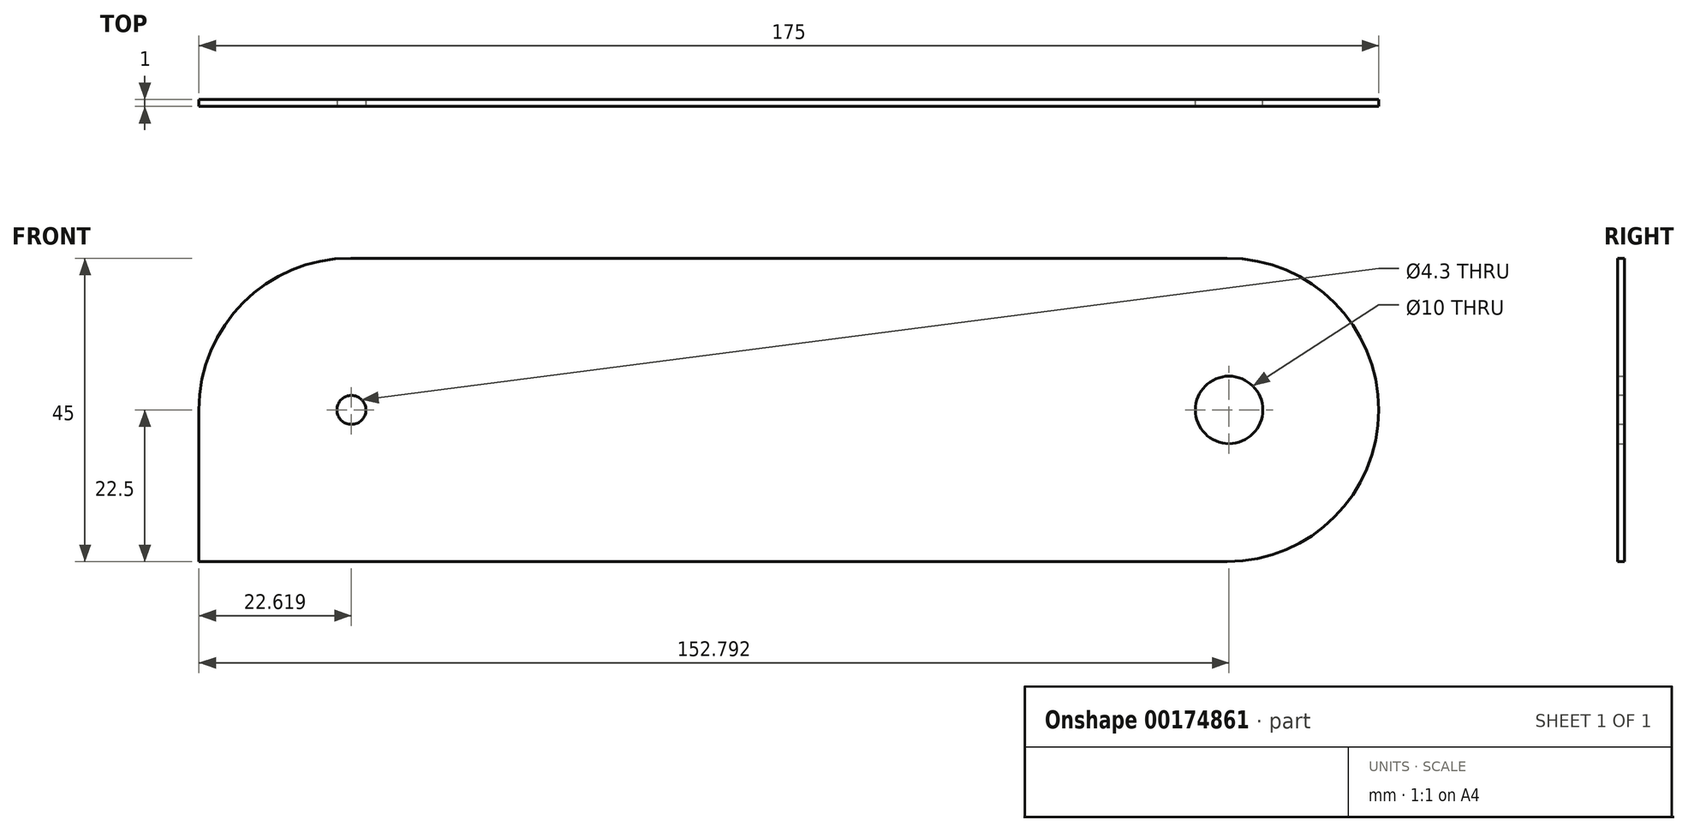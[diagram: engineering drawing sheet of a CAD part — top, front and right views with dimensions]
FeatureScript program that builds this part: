
annotation { "Feature Type Name" : "Feature", "Feature Type Description" : "" }
export const myFeature = defineFeature(function(context is Context, id is Id, definition is map)
    precondition{}
    {
        {
            var Q0;
            Q0=qCreatedBy(makeId("Front.planeOp"),FACE);
            var sketch = newSketch(context, id + "F0", { "sketchPlane" : qUnion([Q0])});
            skLineSegment(sketch, "E0.bottom", {"start": v(82.5, 22.5) * mm, "end": v(-82.5, 22.5) * mm});
            skLineSegment(sketch, "E0.top", {"start": v(82.5, -22.5) * mm, "end": v(-82.5, -22.5) * mm});
            skLineSegment(sketch, "E0.left", {"start": v(82.5, 22.5) * mm, "end": v(82.5, -22.5) * mm});
            skLineSegment(sketch, "E0.right", {"start": v(-82.5, 22.5) * mm, "end": v(-82.5, -22.5) * mm});
            skPoint(sketch, "E0.middle", {"position": v(0, 0) * mm});
            skCircle(sketch, "E1", {"center": v(-65, 0) * mm, "radius": 12.5 * mm});
            skCircle(sketch, "E2", {"center": v(65, 0) * mm, "radius": 12.5 * mm});
            skSolve(sketch);
        }
        {
            var Q0;
            Q0=qSketchRegion(id+"F0",true);
            extrude(context, id + "F1", {"entities" : qUnion([Q0]), "depth" : 1 * mm});
        }
        {
            var Q0;
            Q0=makeQuery(id+"F1.opExtrude","CAP_FACE",FACE,{"disambiguationData":[OSD([sQuery(id+"F0.wireOp",EDGE,"E0.bottom"),sQuery(id+"F0.wireOp",EDGE,"E0.top"),sQuery(id+"F0.wireOp",EDGE,"E0.left"),sQuery(id+"F0.wireOp",EDGE,"E0.right"),sQuery(id+"F0.wireOp",EDGE,"E1"),sQuery(id+"F0.wireOp",EDGE,"E2")])],"isStart":false});
            var sketch = newSketch(context, id + "F2", { "sketchPlane" : qUnion([Q0])});
            skArc(sketch, "E3", {"start": v(65, -22.5) * mm, "mid": v(87.5, 0) * mm, "end": v(65, 22.5) * mm});
            skPoint(sketch, "E4.end.orphan", {"position": v(-82.5, 0) * mm});
            skArc(sketch, "E5", {"start": v(-65, 22.5) * mm, "mid": v(-87.5, 0) * mm, "end": v(-65, -22.5) * mm});
            skLineSegment(sketch, "E6", {"start": v(-65, 22.5) * mm, "end": v(-65, 14.96) * mm});
            skLineSegment(sketch, "E7", {"start": v(-65, 14.96) * mm, "end": v(-75.45, 11.76) * mm});
            skLineSegment(sketch, "E8", {"start": v(-75.45, 11.76) * mm, "end": v(-79.56, 6.47) * mm});
            skLineSegment(sketch, "E9", {"start": v(-79.56, 6.47) * mm, "end": v(-79.56, 0) * mm});
            skLineSegment(sketch, "E10", {"start": v(-79.56, 0) * mm, "end": v(-76.59, -7.8) * mm});
            skLineSegment(sketch, "E11", {"start": v(-76.59, -7.8) * mm, "end": v(-72.84, -12.91) * mm});
            skLineSegment(sketch, "E12", {"start": v(-72.84, -12.91) * mm, "end": v(-67.48, -15.7) * mm});
            skLineSegment(sketch, "E13", {"start": v(-67.48, -15.7) * mm, "end": v(-65, -22.5) * mm});
            skLineSegment(sketch, "E14", {"start": v(65, 22.5) * mm, "end": v(71.47, 16.28) * mm});
            skLineSegment(sketch, "E15", {"start": v(71.47, 16.28) * mm, "end": v(77.4, 9.11) * mm});
            skLineSegment(sketch, "E16", {"start": v(77.4, 9.11) * mm, "end": v(80.4, 2.14) * mm});
            skLineSegment(sketch, "E17", {"start": v(80.4, 2.14) * mm, "end": v(80.4, -5.23) * mm});
            skLineSegment(sketch, "E18", {"start": v(80.4, -5.23) * mm, "end": v(78.4, -12.15) * mm});
            skLineSegment(sketch, "E19", {"start": v(78.4, -12.15) * mm, "end": v(74.66, -14.4) * mm});
            skLineSegment(sketch, "E20", {"start": v(74.66, -14.4) * mm, "end": v(68.4, -19.1) * mm});
            skLineSegment(sketch, "E21", {"start": v(68.4, -19.1) * mm, "end": v(65, -22.5) * mm});
            skSolve(sketch);
        }
        {
            var Q0;
            Q0=qSketchRegion(id+"F2",true);
            extrude(context, id + "F3", {"entities" : qUnion([Q0]), "operationType" : NewBodyOperationType.ADD, "oppositeDirection" : true, "depth" : 1 * mm});
        }
        {
            var Q0;
            {var subQ1=makeQuery(id+"F1.opExtrude","CAP_EDGE",EDGE,{"disambiguationData":[OSD([sQuery(id+"F0.wireOp",EDGE,"E0.bottom")])],"isStart":false});var subQ3=makeQuery(id+"F1.opExtrude","CAP_EDGE",EDGE,{"disambiguationData":[OSD([sQuery(id+"F0.wireOp",EDGE,"E0.right")])],"isStart":false});var subQ5=makeQuery(id+"F2.imprint","INTERSECT",VERTEX,{"derivedFrom":[subQ1,subQ3]});Q0=makeQuery(id+"F2.imprint","IMPRINT",FACE,{"disambiguationData":[TD([[makeQuery(id+"F2.imprint","IMPRINT",EDGE,{"disambiguationData":[TD([[subQ5,-1.0]])],"derivedFrom":subQ3}),1.0]])]});}
            extrude(context, id + "F4", {"entities" : qUnion([Q0]), "operationType" : NewBodyOperationType.REMOVE, "oppositeDirection" : true, "depth" : 25 * mm});
        }
        {
            var Q0;
            {var subQ1=makeQuery(id+"F1.opExtrude","CAP_EDGE",EDGE,{"disambiguationData":[OSD([sQuery(id+"F0.wireOp",EDGE,"E0.top")])],"isStart":false});var subQ3=makeQuery(id+"F1.opExtrude","CAP_EDGE",EDGE,{"disambiguationData":[OSD([sQuery(id+"F0.wireOp",EDGE,"E0.left")])],"isStart":false});var subQ5=makeQuery(id+"F2.imprint","INTERSECT",VERTEX,{"derivedFrom":[subQ1,subQ3]});Q0=makeQuery(id+"F2.imprint","IMPRINT",FACE,{"disambiguationData":[TD([[makeQuery(id+"F2.imprint","IMPRINT",EDGE,{"disambiguationData":[TD([[subQ5,1.0]])],"derivedFrom":subQ3}),-1.0]])]});}
            var Q1;
            {var subQ1=makeQuery(id+"F1.opExtrude","CAP_EDGE",EDGE,{"disambiguationData":[OSD([sQuery(id+"F0.wireOp",EDGE,"E0.bottom")])],"isStart":false});var subQ3=makeQuery(id+"F1.opExtrude","CAP_EDGE",EDGE,{"disambiguationData":[OSD([sQuery(id+"F0.wireOp",EDGE,"E0.left")])],"isStart":false});var subQ5=makeQuery(id+"F2.imprint","INTERSECT",VERTEX,{"derivedFrom":[subQ1,subQ3]});Q1=makeQuery(id+"F2.imprint","IMPRINT",FACE,{"disambiguationData":[TD([[makeQuery(id+"F2.imprint","IMPRINT",EDGE,{"disambiguationData":[TD([[subQ5,-1.0]])],"derivedFrom":subQ3}),-1.0]])]});}
            var Q2;
            {var subQ1=makeQuery(id+"F1.opExtrude","CAP_EDGE",EDGE,{"disambiguationData":[OSD([sQuery(id+"F0.wireOp",EDGE,"E0.top")])],"isStart":false});var subQ3=makeQuery(id+"F1.opExtrude","CAP_EDGE",EDGE,{"disambiguationData":[OSD([sQuery(id+"F0.wireOp",EDGE,"E0.right")])],"isStart":false});var subQ5=makeQuery(id+"F2.imprint","INTERSECT",VERTEX,{"derivedFrom":[subQ1,subQ3]});Q2=makeQuery(id+"F2.imprint","IMPRINT",FACE,{"disambiguationData":[TD([[makeQuery(id+"F2.imprint","IMPRINT",EDGE,{"disambiguationData":[TD([[subQ5,1.0]])],"derivedFrom":subQ3}),1.0]])]});}
            extrude(context, id + "F5", {"entities" : qUnion([Q0, Q1, Q2]), "operationType" : NewBodyOperationType.REMOVE, "oppositeDirection" : true, "depth" : 25 * mm});
        }
        {
            var Q0;
            Q0=makeQuery(id+"F3.boolean.opBoolean","MERGE",FACE,{"derivedFrom":[makeQuery(id+"F1.opExtrude","CAP_FACE",FACE,{"disambiguationData":[OSD([sQuery(id+"F0.wireOp",EDGE,"E0.bottom"),sQuery(id+"F0.wireOp",EDGE,"E0.top"),sQuery(id+"F0.wireOp",EDGE,"E0.left"),sQuery(id+"F0.wireOp",EDGE,"E0.right"),sQuery(id+"F0.wireOp",EDGE,"E1"),sQuery(id+"F0.wireOp",EDGE,"E2")])],"isStart":false}),makeQuery(id+"F3.opExtrude","CAP_FACE",FACE,{"disambiguationData":[OSD([sQuery(id+"F2.wireOp",EDGE,"E3"),sQuery(id+"F2.wireOp",EDGE,"E14"),sQuery(id+"F2.wireOp",EDGE,"E15"),sQuery(id+"F2.wireOp",EDGE,"E16"),sQuery(id+"F2.wireOp",EDGE,"E17"),sQuery(id+"F2.wireOp",EDGE,"E18"),sQuery(id+"F2.wireOp",EDGE,"E19"),sQuery(id+"F2.wireOp",EDGE,"E20"),sQuery(id+"F2.wireOp",EDGE,"E21")])],"isStart":true}),makeQuery(id+"F3.opExtrude","CAP_FACE",FACE,{"disambiguationData":[OSD([sQuery(id+"F2.wireOp",EDGE,"E5"),sQuery(id+"F2.wireOp",EDGE,"E6"),sQuery(id+"F2.wireOp",EDGE,"E7"),sQuery(id+"F2.wireOp",EDGE,"E8"),sQuery(id+"F2.wireOp",EDGE,"E9"),sQuery(id+"F2.wireOp",EDGE,"E10"),sQuery(id+"F2.wireOp",EDGE,"E11"),sQuery(id+"F2.wireOp",EDGE,"E12"),sQuery(id+"F2.wireOp",EDGE,"E13")])],"isStart":true})]});
            var sketch = newSketch(context, id + "F6", { "sketchPlane" : qUnion([Q0])});
            skCircle(sketch, "E22", {"center": v(-65, 0) * mm, "radius": 12.5 * mm});
            skCircle(sketch, "E23", {"center": v(-65, 0) * mm, "radius": 13.5 * mm});
            skCircle(sketch, "E24", {"center": v(65, 0) * mm, "radius": 12.5 * mm});
            skCircle(sketch, "E25", {"center": v(65, 0) * mm, "radius": 13.5 * mm});
            skSolve(sketch);
        }
        {
            var Q0;
            Q0=makeQuery(id+"F3.boolean.opBoolean","MERGE",FACE,{"derivedFrom":[makeQuery(id+"F1.opExtrude","CAP_FACE",FACE,{"disambiguationData":[OSD([sQuery(id+"F0.wireOp",EDGE,"E0.bottom"),sQuery(id+"F0.wireOp",EDGE,"E0.top"),sQuery(id+"F0.wireOp",EDGE,"E0.left"),sQuery(id+"F0.wireOp",EDGE,"E0.right"),sQuery(id+"F0.wireOp",EDGE,"E1"),sQuery(id+"F0.wireOp",EDGE,"E2")])],"isStart":false}),makeQuery(id+"F3.opExtrude","CAP_FACE",FACE,{"disambiguationData":[OSD([sQuery(id+"F2.wireOp",EDGE,"E3"),sQuery(id+"F2.wireOp",EDGE,"E14"),sQuery(id+"F2.wireOp",EDGE,"E15"),sQuery(id+"F2.wireOp",EDGE,"E16"),sQuery(id+"F2.wireOp",EDGE,"E17"),sQuery(id+"F2.wireOp",EDGE,"E18"),sQuery(id+"F2.wireOp",EDGE,"E19"),sQuery(id+"F2.wireOp",EDGE,"E20"),sQuery(id+"F2.wireOp",EDGE,"E21")])],"isStart":true}),makeQuery(id+"F3.opExtrude","CAP_FACE",FACE,{"disambiguationData":[OSD([sQuery(id+"F2.wireOp",EDGE,"E5"),sQuery(id+"F2.wireOp",EDGE,"E6"),sQuery(id+"F2.wireOp",EDGE,"E7"),sQuery(id+"F2.wireOp",EDGE,"E8"),sQuery(id+"F2.wireOp",EDGE,"E9"),sQuery(id+"F2.wireOp",EDGE,"E10"),sQuery(id+"F2.wireOp",EDGE,"E11"),sQuery(id+"F2.wireOp",EDGE,"E12"),sQuery(id+"F2.wireOp",EDGE,"E13")])],"isStart":true})]});
            var sketch = newSketch(context, id + "F7", { "sketchPlane" : qUnion([Q0])});
            skLineSegment(sketch, "E26.bottom", {"start": v(-87.5, 0) * mm, "end": v(-81.94, 0) * mm});
            skLineSegment(sketch, "E26.top", {"start": v(-87.5, -22.5) * mm, "end": v(-65, -22.5) * mm});
            skLineSegment(sketch, "E26.left", {"start": v(-87.5, 0) * mm, "end": v(-87.5, -22.5) * mm});
            skLineSegment(sketch, "E26.right", {"start": v(-65, -18.59) * mm, "end": v(-65, -22.5) * mm});
            skLineSegment(sketch, "E27", {"start": v(-81.94, 0) * mm, "end": v(-80.2, -9.62) * mm});
            skLineSegment(sketch, "E28", {"start": v(-80.2, -9.62) * mm, "end": v(-73.32, -16) * mm});
            skLineSegment(sketch, "E29", {"start": v(-73.32, -16) * mm, "end": v(-65, -18.59) * mm});
            skSolve(sketch);
        }
        {
            var Q0;
            Q0=qSketchRegion(id+"F7",true);
            extrude(context, id + "F8", {"entities" : qUnion([Q0]), "operationType" : NewBodyOperationType.ADD, "oppositeDirection" : true, "depth" : 1 * mm});
        }
        {
            var Q0;
            Q0=makeQuery(id+"F8.boolean.opBoolean","MERGE",FACE,{"derivedFrom":[makeQuery(id+"F3.boolean.opBoolean","MERGE",FACE,{"derivedFrom":[makeQuery(id+"F1.opExtrude","CAP_FACE",FACE,{"disambiguationData":[OSD([sQuery(id+"F0.wireOp",EDGE,"E0.bottom"),sQuery(id+"F0.wireOp",EDGE,"E0.top"),sQuery(id+"F0.wireOp",EDGE,"E0.left"),sQuery(id+"F0.wireOp",EDGE,"E0.right"),sQuery(id+"F0.wireOp",EDGE,"E1"),sQuery(id+"F0.wireOp",EDGE,"E2")])],"isStart":false}),makeQuery(id+"F3.opExtrude","CAP_FACE",FACE,{"disambiguationData":[OSD([sQuery(id+"F2.wireOp",EDGE,"E3"),sQuery(id+"F2.wireOp",EDGE,"E14"),sQuery(id+"F2.wireOp",EDGE,"E15"),sQuery(id+"F2.wireOp",EDGE,"E16"),sQuery(id+"F2.wireOp",EDGE,"E17"),sQuery(id+"F2.wireOp",EDGE,"E18"),sQuery(id+"F2.wireOp",EDGE,"E19"),sQuery(id+"F2.wireOp",EDGE,"E20"),sQuery(id+"F2.wireOp",EDGE,"E21")])],"isStart":true}),makeQuery(id+"F3.opExtrude","CAP_FACE",FACE,{"disambiguationData":[OSD([sQuery(id+"F2.wireOp",EDGE,"E5"),sQuery(id+"F2.wireOp",EDGE,"E6"),sQuery(id+"F2.wireOp",EDGE,"E7"),sQuery(id+"F2.wireOp",EDGE,"E8"),sQuery(id+"F2.wireOp",EDGE,"E9"),sQuery(id+"F2.wireOp",EDGE,"E10"),sQuery(id+"F2.wireOp",EDGE,"E11"),sQuery(id+"F2.wireOp",EDGE,"E12"),sQuery(id+"F2.wireOp",EDGE,"E13")])],"isStart":true})]}),makeQuery(id+"F8.opExtrude","CAP_FACE",FACE,{"disambiguationData":[OSD([sQuery(id+"F7.wireOp",EDGE,"E26.bottom"),sQuery(id+"F7.wireOp",EDGE,"E26.top"),sQuery(id+"F7.wireOp",EDGE,"E26.left"),sQuery(id+"F7.wireOp",EDGE,"E26.right"),sQuery(id+"F7.wireOp",EDGE,"E27"),sQuery(id+"F7.wireOp",EDGE,"E28"),sQuery(id+"F7.wireOp",EDGE,"E29")])],"isStart":true})]});
            var sketch = newSketch(context, id + "F9", { "sketchPlane" : qUnion([Q0])});
            skLineSegment(sketch, "E30.bottom", {"start": v(-42.87, 16.23) * mm, "end": v(-78.86, 16.23) * mm});
            skLineSegment(sketch, "E30.top", {"start": v(-42.87, -15.15) * mm, "end": v(-78.86, -15.15) * mm});
            skLineSegment(sketch, "E30.left", {"start": v(-42.87, 16.23) * mm, "end": v(-42.87, -15.15) * mm});
            skLineSegment(sketch, "E30.right", {"start": v(-78.86, 16.23) * mm, "end": v(-78.86, -15.15) * mm});
            skLineSegment(sketch, "E31.bottom", {"start": v(46.87, 14.52) * mm, "end": v(80.55, 14.52) * mm});
            skLineSegment(sketch, "E31.top", {"start": v(46.87, -14.3) * mm, "end": v(80.55, -14.3) * mm});
            skLineSegment(sketch, "E31.left", {"start": v(46.87, 14.52) * mm, "end": v(46.87, -14.3) * mm});
            skLineSegment(sketch, "E31.right", {"start": v(80.55, 14.52) * mm, "end": v(80.55, -14.3) * mm});
            skSolve(sketch);
        }
        {
            var Q0;
            Q0 = qSketchRegion(id + "F9", true);
            extrude(context, id + "F10", {"entities" : qUnion([Q0]), "operationType" : NewBodyOperationType.ADD, "oppositeDirection" : true, "depth" : 1 * mm});
        }
        {
            var Q0;
            Q0=makeQuery(id+"F6.imprint","IMPRINT",FACE,{"disambiguationData":[TD([[makeQuery(id+"F6.imprint","IMPRINT",EDGE,{"derivedFrom":sQuery(id+"F6.wireOp",EDGE,"E24")}),1.0]])]});
            var sketch = newSketch(context, id + "F11", { "sketchPlane" : qUnion([Q0])});
            skCircle(sketch, "E32", {"center": v(65.3, 0) * mm, "radius": 4.12 * mm});
            skSolve(sketch);
        }
        {
            var Q0;
            Q0 = qSketchRegion(id + "F11", true);
            extrude(context, id + "F12", {"entities" : qUnion([Q0]), "operationType" : NewBodyOperationType.REMOVE, "oppositeDirection" : true, "depth" : 25 * mm});
        }
        {
            var Q0;
            Q0=makeQuery(id+"F6.imprint","IMPRINT",FACE,{"disambiguationData":[TD([[makeQuery(id+"F6.imprint","IMPRINT",EDGE,{"derivedFrom":sQuery(id+"F6.wireOp",EDGE,"E23")}),-1.0]])]});
            var sketch = newSketch(context, id + "F13", { "sketchPlane" : qUnion([Q0])});
            skCircle(sketch, "E33", {"center": v(-64.88, 0) * mm, "radius": 2.15 * mm});
            skSolve(sketch);
        }
        {
            var Q0;
            Q0 = qSketchRegion(id + "F13", true);
            extrude(context, id + "F14", {"entities" : qUnion([Q0]), "operationType" : NewBodyOperationType.REMOVE, "oppositeDirection" : true, "depth" : 25 * mm});
        }
        {
            var Q0;
            Q0=makeQuery(id+"F10.boolean.opBoolean","MERGE",FACE,{"derivedFrom":[makeQuery(id+"F8.boolean.opBoolean","MERGE",FACE,{"derivedFrom":[makeQuery(id+"F3.boolean.opBoolean","MERGE",FACE,{"derivedFrom":[makeQuery(id+"F1.opExtrude","CAP_FACE",FACE,{"disambiguationData":[OSD([sQuery(id+"F0.wireOp",EDGE,"E0.bottom"),sQuery(id+"F0.wireOp",EDGE,"E0.top"),sQuery(id+"F0.wireOp",EDGE,"E0.left"),sQuery(id+"F0.wireOp",EDGE,"E0.right"),sQuery(id+"F0.wireOp",EDGE,"E1"),sQuery(id+"F0.wireOp",EDGE,"E2")])],"isStart":true}),makeQuery(id+"F3.opExtrude","CAP_FACE",FACE,{"disambiguationData":[OSD([sQuery(id+"F2.wireOp",EDGE,"E3"),sQuery(id+"F2.wireOp",EDGE,"E14"),sQuery(id+"F2.wireOp",EDGE,"E15"),sQuery(id+"F2.wireOp",EDGE,"E16"),sQuery(id+"F2.wireOp",EDGE,"E17"),sQuery(id+"F2.wireOp",EDGE,"E18"),sQuery(id+"F2.wireOp",EDGE,"E19"),sQuery(id+"F2.wireOp",EDGE,"E20"),sQuery(id+"F2.wireOp",EDGE,"E21")])],"isStart":false}),makeQuery(id+"F3.opExtrude","CAP_FACE",FACE,{"disambiguationData":[OSD([sQuery(id+"F2.wireOp",EDGE,"E5"),sQuery(id+"F2.wireOp",EDGE,"E6"),sQuery(id+"F2.wireOp",EDGE,"E7"),sQuery(id+"F2.wireOp",EDGE,"E8"),sQuery(id+"F2.wireOp",EDGE,"E9"),sQuery(id+"F2.wireOp",EDGE,"E10"),sQuery(id+"F2.wireOp",EDGE,"E11"),sQuery(id+"F2.wireOp",EDGE,"E12"),sQuery(id+"F2.wireOp",EDGE,"E13")])],"isStart":false})]}),makeQuery(id+"F8.opExtrude","CAP_FACE",FACE,{"disambiguationData":[OSD([sQuery(id+"F7.wireOp",EDGE,"E26.bottom"),sQuery(id+"F7.wireOp",EDGE,"E26.top"),sQuery(id+"F7.wireOp",EDGE,"E26.left"),sQuery(id+"F7.wireOp",EDGE,"E26.right"),sQuery(id+"F7.wireOp",EDGE,"E27"),sQuery(id+"F7.wireOp",EDGE,"E28"),sQuery(id+"F7.wireOp",EDGE,"E29")])],"isStart":false})]}),makeQuery(id+"F10.opExtrude","CAP_FACE",FACE,{"disambiguationData":[OSD([sQuery(id+"F9.wireOp",EDGE,"E30.bottom"),sQuery(id+"F9.wireOp",EDGE,"E30.top"),sQuery(id+"F9.wireOp",EDGE,"E30.left"),sQuery(id+"F9.wireOp",EDGE,"E30.right")])],"isStart":false}),makeQuery(id+"F10.opExtrude","CAP_FACE",FACE,{"disambiguationData":[OSD([sQuery(id+"F9.wireOp",EDGE,"E31.bottom"),sQuery(id+"F9.wireOp",EDGE,"E31.top"),sQuery(id+"F9.wireOp",EDGE,"E31.left"),sQuery(id+"F9.wireOp",EDGE,"E31.right")])],"isStart":false})]});
            var sketch = newSketch(context, id + "F15", { "sketchPlane" : qUnion([Q0])});
            skCircle(sketch, "E34", {"center": v(-65.3, 0) * mm, "radius": 5 * mm});
            skSolve(sketch);
        }
        {
            var Q0;
            Q0 = qSketchRegion(id + "F15", true);
            extrude(context, id + "F16", {"entities" : qUnion([Q0]), "operationType" : NewBodyOperationType.REMOVE, "oppositeDirection" : true, "depth" : 25 * mm});
        }
    });
